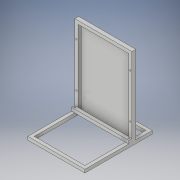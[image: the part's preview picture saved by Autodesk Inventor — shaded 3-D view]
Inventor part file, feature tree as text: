
AUTODESK INVENTOR PART (.ipt)
format: ipt  version: 2019 (Build 230136000, 136)  size: 197,120 bytes
history: native  units: mm
features: extrude x7, sketch x7
ambient origin geometry x8: Origin, YZ Plane, XZ Plane, XY Plane, X Axis, Y Axis, Z Axis, Center Point
bodies: Solid1 (feature_tree)
feature tree (14):
  extrude  "Extrusion1"  Depth=19.0mm
  extrude  "Extrusion2"  Depth=19.0mm
  extrude  "Extrusion3"  Depth=335.0mm
  extrude  "Extrusion4"  Depth=19.0mm
  extrude  "Extrusion5"  Depth=100.0mm
  extrude  "Extrusion6"  Depth=19.0mm
  extrude  "Extrusion7"  Depth=4.0mm
  sketch  "Sketch1"  dims[d2=19.0mm d3=19.0mm]
  sketch  "Sketch3"  dims[d4=19.0mm d5=19.0mm]
  sketch  "Sketch4"  dims[d6=395.0mm d7=335.0mm]
  sketch  "Sketch5"  dims[d8=19.0mm d9=0.0mm d26=19.0mm]
  sketch  "Sketch6"  dims[d27=19.0mm d28=100.0mm]
  sketch  "Sketch7"  dims[d29=460.0mm d30=0.0mm d31=19.0mm]
  sketch  "Sketch8"  dims[d32=316.0mm d33=0.0mm d34=8.0mm d35=8.0mm d36=8.0mm d37=8.0mm d38=9.5mm d39=100.0mm d40=100.0mm d41=9.5mm d42=9.5mm d43=100.0mm d44=100.0mm d45=9.5mm d46=19.0mm d47=0.0mm d48=19.0mm d49=335.0mm d51=119.0mm d52=19.0mm d53=0.0mm d54=8.0mm d55=8.0mm d56=9.5mm d57=9.5mm d58=9.5mm d59=9.5mm d60=39.0mm d61=0.0mm d62=4.0mm d63=0.0mm]
